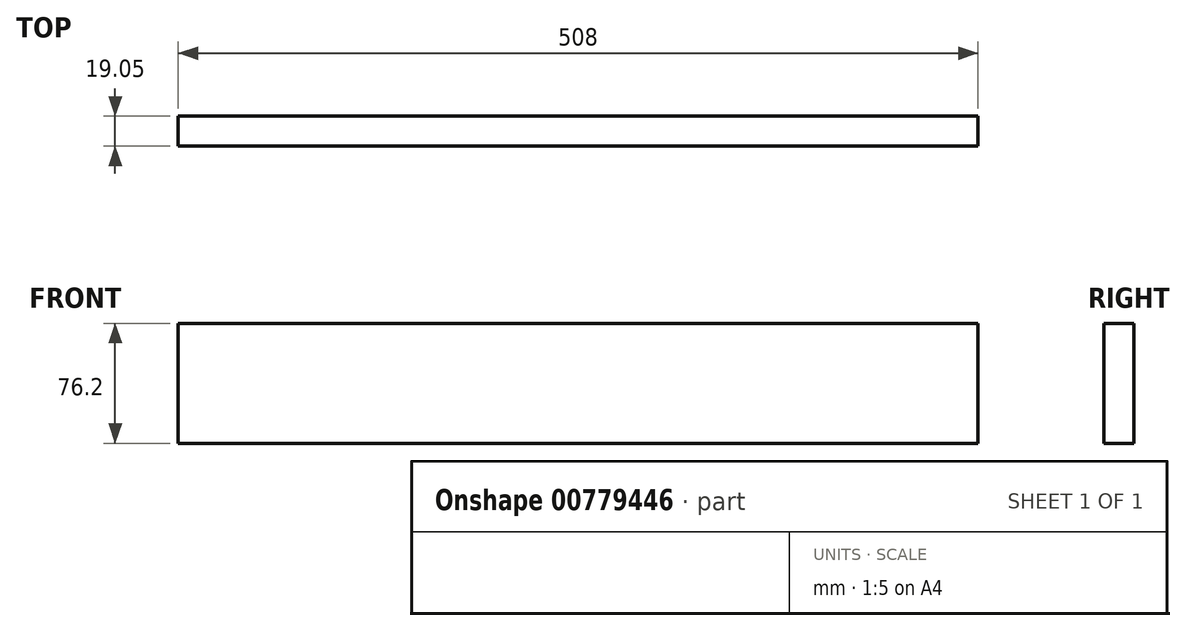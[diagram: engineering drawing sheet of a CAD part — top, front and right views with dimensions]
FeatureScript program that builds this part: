
annotation { "Feature Type Name" : "Feature", "Feature Type Description" : "" }
export const myFeature = defineFeature(function(context is Context, id is Id, definition is map)
    precondition{}
    {
        {
            var Q0;
            Q0=qCreatedBy(makeId("Front.planeOp"),FACE);
            var sketch = newSketch(context, id + "F0", { "sketchPlane" : qUnion([Q0])});
            skLineSegment(sketch, "E0.bottom", {"start": v(-254, 38.1) * mm, "end": v(254, 38.1) * mm});
            skLineSegment(sketch, "E0.top", {"start": v(-254, -38.1) * mm, "end": v(254, -38.1) * mm});
            skLineSegment(sketch, "E0.left", {"start": v(-254, 38.1) * mm, "end": v(-254, -38.1) * mm});
            skLineSegment(sketch, "E0.right", {"start": v(254, 38.1) * mm, "end": v(254, -38.1) * mm});
            skPoint(sketch, "E0.middle", {"position": v(0, 0) * mm});
            skSolve(sketch);
        }
        {
            var Q0;
            Q0=makeQuery(id+"F0.imprint","IMPRINT",FACE,{"disambiguationData":[TD([[makeQuery(id+"F0.imprint","IMPRINT",EDGE,{"derivedFrom":sQuery(id+"F0.wireOp",EDGE,"E0.bottom")}),-1.0]])]});
            extrude(context, id + "F1", {"entities" : qUnion([Q0]), "depth" : 19.05 * mm, "offsetDistance" : 25.4 * mm});
        }
    });
